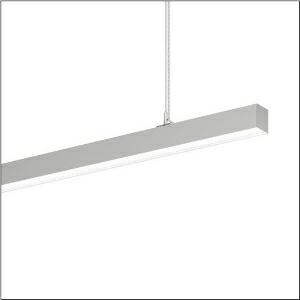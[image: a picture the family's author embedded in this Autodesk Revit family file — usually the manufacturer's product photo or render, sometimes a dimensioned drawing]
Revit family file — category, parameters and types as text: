
# Revit family: silica_r__21_51mx30tat4s_875d
name_source: partatom
category: Lighting Fixtures
units: mm (PartAtom-declared; Revit-internal decimal feet)

## family parameters
Cut with Voids When Loaded = No
Host = Face
Light Source = No
Part Type = Normal
Room Calculation Point = No
Round Connector Dimension = Use Diameter
Shared = No

## types (1)
- --- (1 x LED, 4120 lm, 33.8 W, 6500K)
    Apparent Load = 34 VA
    CIE Flux Codes = 47 79 96 58 100
    Color Rendering = 80
    Color Temperature = 6500K
    Default Elevation = 1800 mm
    Description = Silica® 21, office luminaire, primary optical cover: cover, of PMMA, opal, light emission: direct/indirect distribution, primary light characteristic: symmetric, installation type: suspended mounting, LED, rated luminous flux: 4.120lm, luminous efficacy: 116lm/W, light colour: 8tw, colour temperature: 2700..6500K, control gear: DALI DT8, with terminal, 3+2-pole, max. 2.5mm², mains connection: 220..240V, AC, 50/60Hz, rated input power: 35.5W, luminaire housing, of aluminium, metallic grey (RAL 9006), length: 1.204mm, width: 53mm, height: 53mm, protection rating (complete): IP20, insulation class (complete): insulation class I (protective earthing), certification: CE, permissible operating ambient temperature: 0..+35°C, standard: EN 50419, packaging unit: 1 piece
    Height = 53 mm
    Lamp = 1 x LED
    Lamp Light Flux = 4120 lm
    Lamp Power = 33.8 W
    Lamp count = 1
    Length = 1204 mm
    Luminous efficacy = 122 lm/W
    Manufacturer = Siteco
    ModVariant = No
    Model = 51MX30TAT4S
    Mounting Place = Ceiling
    Mounting Type = Pendant
    Number of Poles = 1
    OnlyDefault = Yes
    Power Factor = 1
    Product Name = Silica® 21
    Product group = office luminaire | ceiling pendant
    ProductGroupID = 904
    Protection Class = Protection class I
    Protection Degree = IP 20
    RLX_Detail_Level = 1
    RLX_Emergency_Light_Flux = 0 lm
    RLX_Emergency_Type = 0
    RLX_Emergency_Type_DB = No
    RlxData = <blob elided: 20137 chars, md5=39bbeecb>
    Socket = socket
    Standby Power = 0 W
    System Light Flux = 4120 lm
    System Power = 34 W
    Type Comments = individual setting
    Type Image = l_1335864.jpg
    URL = http://relux.com
    VarID = @adj_139620
    Voltage = 0 V
    Weight = 0.00 kg
    Width = 53 mm

## geometry (parser evidence)
native form markers: Blend x4, Sweep x13
no freeform markers — native parametric forms only
